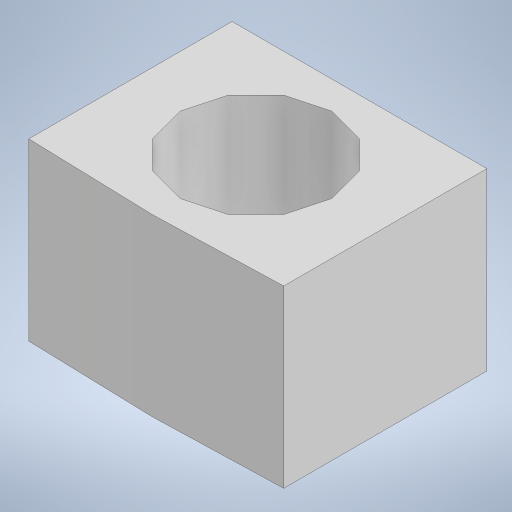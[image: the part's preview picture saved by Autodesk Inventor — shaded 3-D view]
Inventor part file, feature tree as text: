
AUTODESK INVENTOR PART (.ipt)
format: ipt  version: 2024 (Build 280153000, 153)  size: 487,936 bytes
history: native  units: mm
features: extrude x1, sketch x1
ambient origin geometry x8: Origin, YZ Plane, XZ Plane, XY Plane, X Axis, Y Axis, Z Axis, Center Point
bodies: Solid1 (feature_tree)
feature tree (2):
  extrude  "Extrusion1"  Depth=5.5mm
  sketch  "Sketch1"  dims[d0=170.0mm d1=109.0mm d2=105.5mm d3=166.5mm d4=160.0mm d5=4.75mm d6=3.25mm d7=4.0mm d8=4.0mm d9=163.25mm d10=5.5mm d11=0.0mm]
